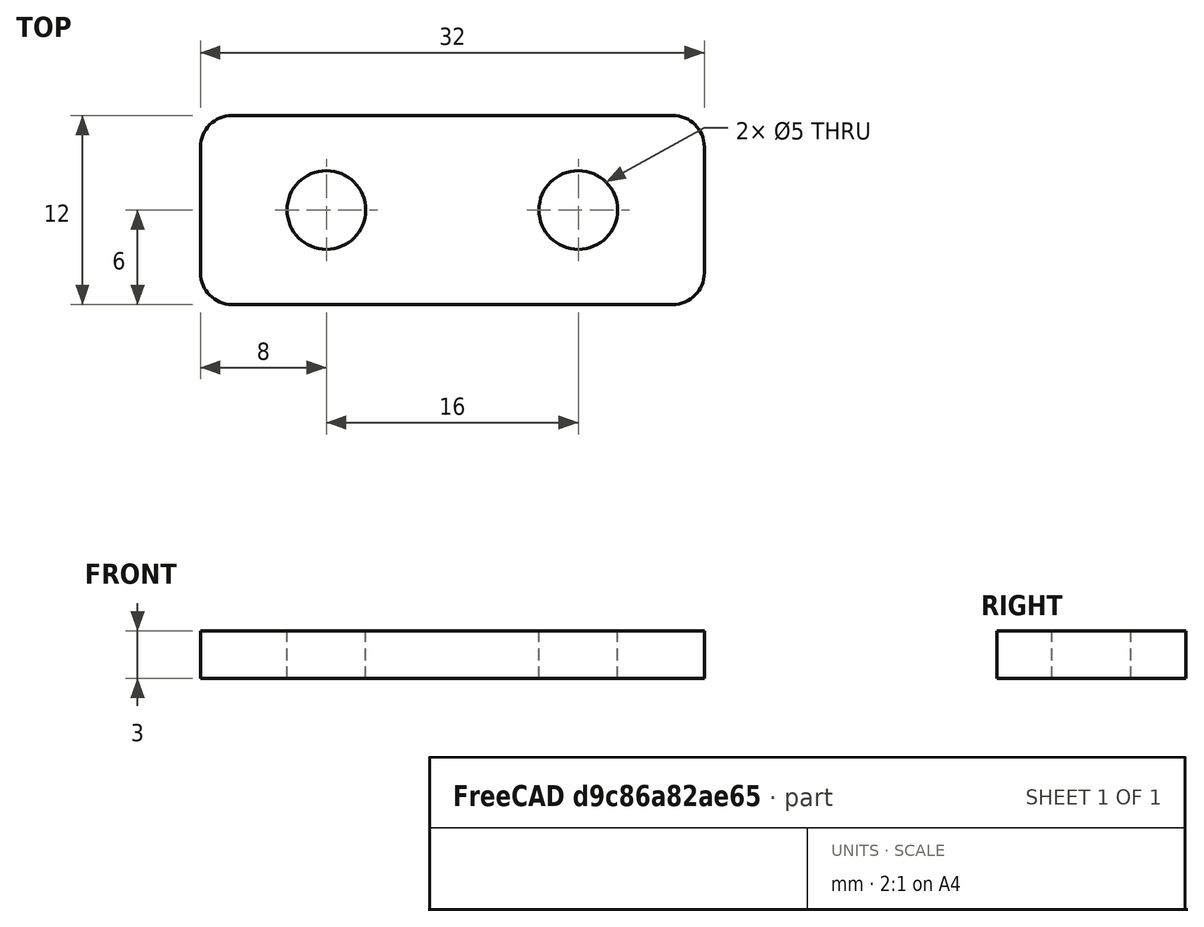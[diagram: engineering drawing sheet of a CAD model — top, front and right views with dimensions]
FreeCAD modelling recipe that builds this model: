
FCSTD DOCUMENT  (FreeCAD 0.17R13541 (Git))
Label: SujetaCable16mm
License: All rights reserved
LicenseURL: http://en.wikipedia.org/wiki/All_rights_reserved
objects: Part::Cylinder×2, Part::Box×1, Part::MultiFuse×1, Part::Cut×1, Part::Fillet×1, Part::Feature×1
note: 7 computed .brp shape members not serialized (recipe doc carries the construction recipe); baked Part::Feature solids carry a one-line shape summary decoded from their .brp

FEATURE [Part::Box] Box  label="Cubo"
  AttacherType = Attacher::AttachEngine3D
  Height = 3
  Length = 32
  Width = 12
FEATURE [Part::Cylinder] Cylinder  label="Cilindro"
  Angle = 360
  AttacherType = Attacher::AttachEngine3D
  Height = 10
  Placement = pos=(8,6,0) rot=(0,0,1;0rad)
  Radius = 2.5
FEATURE [Part::Cylinder] Cylinder001  label="Cilindro001"
  Angle = 360
  AttacherType = Attacher::AttachEngine3D
  Height = 10
  Placement = pos=(24,6,0) rot=(0,0,1;0rad)
  Radius = 2.5
FEATURE [Part::MultiFuse] Fusion
  Refine = true
  Shapes = -> [Cylinder001,Cylinder]
FEATURE [Part::Cut] Cut
  Base = -> Box
  Refine = true
  Tool = -> Fusion
FEATURE [Part::Fillet] Fillet  label="SujetaCable16mm-Terminado"
  Base = -> Cut
  Edges = 4 edges r=2: [Edge1,Edge3,Edge6,Edge13]
FEATURE [Part::Feature] Fillet001  label="SujetaCable16mm-CopiaSimple"
  shape: bbox 32 x 12 x 3 mm, 12 faces (baked)
